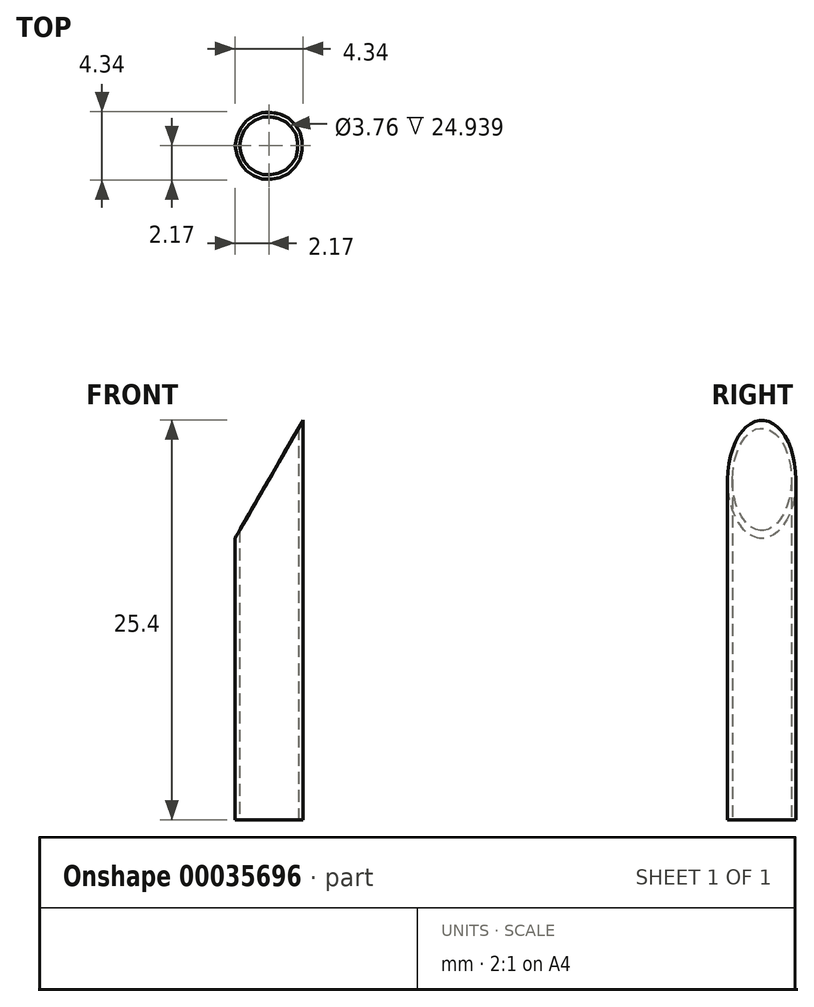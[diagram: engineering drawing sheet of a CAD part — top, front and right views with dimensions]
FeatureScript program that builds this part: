
annotation { "Feature Type Name" : "Feature", "Feature Type Description" : "" }
export const myFeature = defineFeature(function(context is Context, id is Id, definition is map)
    precondition{}
    {
        {
            var Q0;
            Q0=qCreatedBy(makeId("Front.planeOp"),FACE);
            var sketch = newSketch(context, id + "F0", { "sketchPlane" : qUnion([Q0])});
            skLineSegment(sketch, "E0", {"start": v(0, 0) * mm, "end": v(0, 25.4) * mm});
            skLineSegment(sketch, "E1", {"start": v(0, 25.4) * mm, "end": v(1.88, 25.4) * mm});
            skLineSegment(sketch, "E2", {"start": v(1.88, 25.4) * mm, "end": v(1.88, 0) * mm});
            skLineSegment(sketch, "E3", {"start": v(1.88, 0) * mm, "end": v(0, 0) * mm});
            skLineSegment(sketch, "E4", {"start": v(1.88, 0) * mm, "end": v(2.17, 0) * mm});
            skLineSegment(sketch, "E5", {"start": v(2.17, 0) * mm, "end": v(2.17, 25.4) * mm});
            skLineSegment(sketch, "E6", {"start": v(2.17, 25.4) * mm, "end": v(1.88, 25.4) * mm});
            skSolve(sketch);
        }
        {
            var Q0;
            Q0=makeQuery(id+"F0.imprint","IMPRINT",FACE,{"disambiguationData":[TD([[makeQuery(id+"F0.imprint","IMPRINT",EDGE,{"derivedFrom":sQuery(id+"F0.wireOp",EDGE,"E2")}),1.0]])]});
            var Q1;
            Q1=sQuery(id+"F0.wireOp",EDGE,"E0");
            revolve(context, id + "F1", {"entities" : qUnion([Q0]), "axis" : qUnion([Q1]), "revolveType" : RevolveType.FULL});
        }
        {
            var Q0;
            Q0=qCreatedBy(makeId("Front.planeOp"),FACE);
            var sketch = newSketch(context, id + "F2", { "sketchPlane" : qUnion([Q0])});
            skLineSegment(sketch, "E7.0", {"start": v(2.17, 25.4) * mm, "end": v(-2.17, 25.4) * mm});
            skLineSegment(sketch, "E8", {"start": v(-2.17, 25.4) * mm, "end": v(-2.17, 17.88) * mm});
            skLineSegment(sketch, "E9", {"start": v(-2.17, 17.88) * mm, "end": v(-4.71, 17.88) * mm});
            skLineSegment(sketch, "E10", {"start": v(-4.71, 17.88) * mm, "end": v(-4.71, 27.94) * mm});
            skLineSegment(sketch, "E11", {"start": v(-4.71, 27.94) * mm, "end": v(2.17, 27.94) * mm});
            skLineSegment(sketch, "E12", {"start": v(2.17, 27.94) * mm, "end": v(2.17, 25.4) * mm});
            skLineSegment(sketch, "E13", {"start": v(2.17, 25.4) * mm, "end": v(-2.17, 17.88) * mm});
            skSolve(sketch);
        }
        {
            var Q0;
            Q0=makeQuery(id+"F2.imprint","IMPRINT",FACE,{"disambiguationData":[TD([[makeQuery(id+"F2.imprint","IMPRINT",EDGE,{"derivedFrom":sQuery(id+"F2.wireOp",EDGE,"E7.0")}),-1.0]])]});
            var Q1;
            Q1=makeQuery(id+"F2.imprint","IMPRINT",FACE,{"disambiguationData":[TD([[makeQuery(id+"F2.imprint","IMPRINT",EDGE,{"derivedFrom":sQuery(id+"F2.wireOp",EDGE,"E7.0")}),1.0]])]});
            extrude(context, id + "F3", {"entities" : qUnion([Q0, Q1]), "operationType" : NewBodyOperationType.REMOVE, "oppositeDirection" : true, "depth" : 25.4 * mm, "symmetric" : true});
        }
    });
